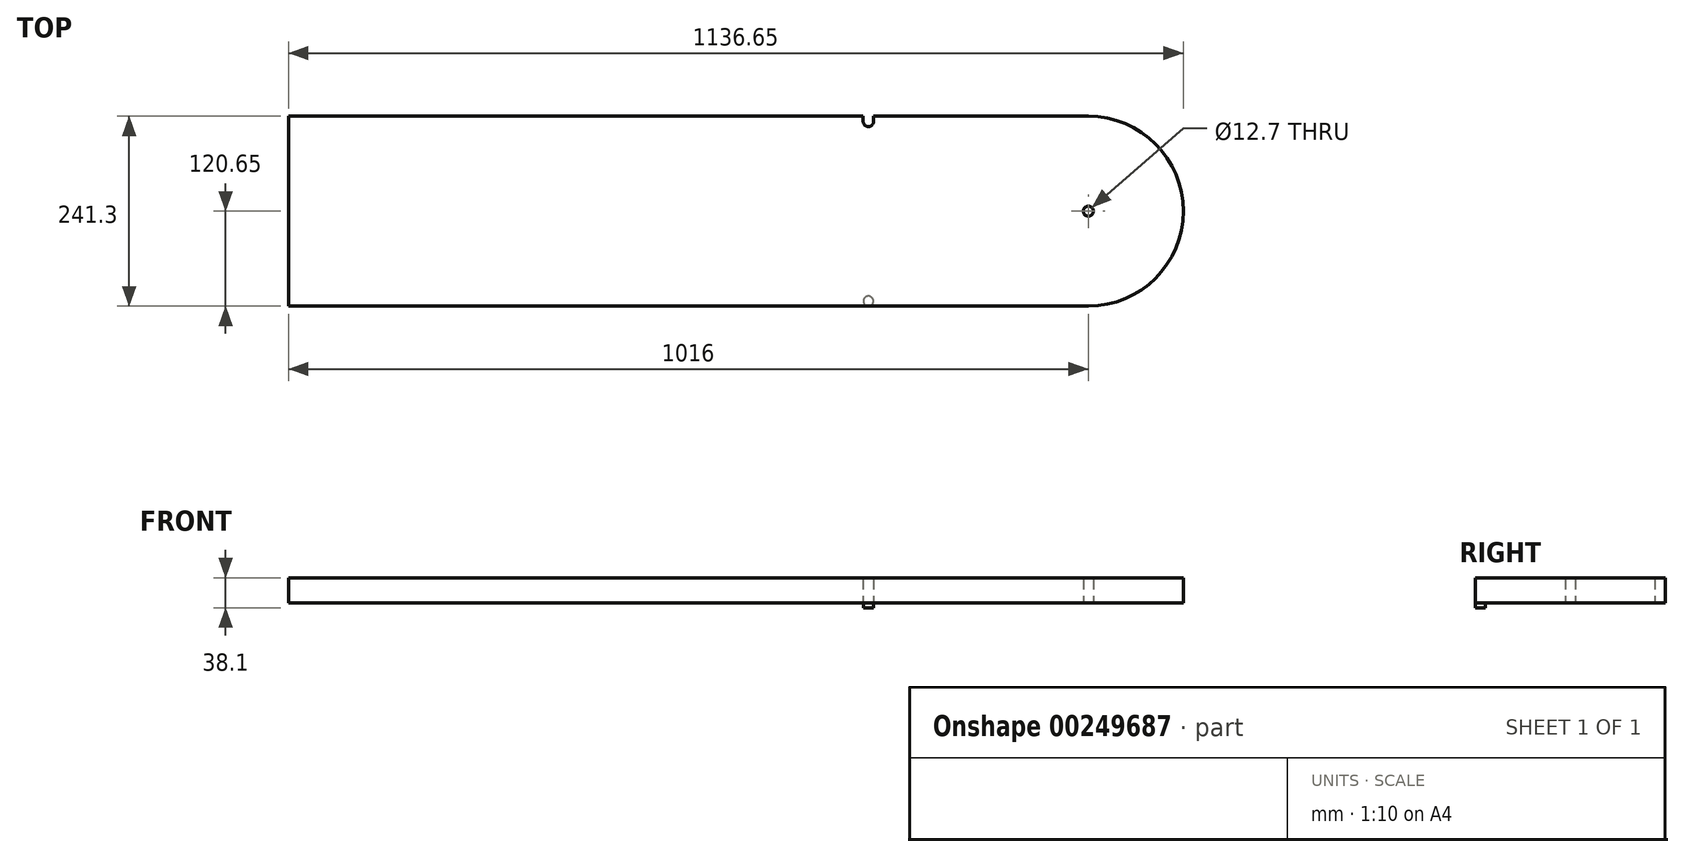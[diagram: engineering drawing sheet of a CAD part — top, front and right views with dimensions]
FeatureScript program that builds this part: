
annotation { "Feature Type Name" : "Feature", "Feature Type Description" : "" }
export const myFeature = defineFeature(function(context is Context, id is Id, definition is map)
    precondition{}
    {
        {
            var Q0;
            Q0=qCreatedBy(makeId("Top.planeOp"),FACE);
            var sketch = newSketch(context, id + "F0", { "sketchPlane" : qUnion([Q0])});
            skLineSegment(sketch, "E0.bottom", {"start": v(-1136.65, -120.65) * mm, "end": v(-120.65, -120.65) * mm});
            skLineSegment(sketch, "E0.top", {"start": v(-1136.65, 120.65) * mm, "end": v(-120.65, 120.65) * mm});
            skLineSegment(sketch, "E0.left", {"start": v(-1136.65, -120.65) * mm, "end": v(-1136.65, 120.65) * mm});
            skArc(sketch, "E1", {"start": v(-120.65, -120.65) * mm, "mid": v(0, 0) * mm, "end": v(-120.65, 120.65) * mm});
            skCircle(sketch, "E2", {"center": v(-120.65, 0) * mm, "radius": 6.35 * mm});
            skSolve(sketch);
        }
        {
            var Q0;
            Q0 = qSketchRegion(id + "F0", true);
            extrude(context, id + "F1", {"entities" : qUnion([Q0]), "depth" : 31.75 * mm});
        }
        {
            var Q0;
            Q0=makeQuery(id+"F1.opExtrude","CAP_FACE",FACE,{"disambiguationData":[OSD([sQuery(id+"F0.wireOp",EDGE,"E0.bottom"),sQuery(id+"F0.wireOp",EDGE,"E0.top"),sQuery(id+"F0.wireOp",EDGE,"E0.left"),sQuery(id+"F0.wireOp",EDGE,"E1"),sQuery(id+"F0.wireOp",EDGE,"E2")])],"isStart":true});
            var sketch = newSketch(context, id + "F2", { "sketchPlane" : qUnion([Q0])});
            skCircle(sketch, "E3", {"center": v(-400.05, 114.3) * mm, "radius": 6.35 * mm});
            skSolve(sketch);
        }
        {
            var Q0;
            Q0 = qSketchRegion(id + "F2", true);
            extrude(context, id + "F3", {"entities" : qUnion([Q0]), "operationType" : NewBodyOperationType.ADD, "depth" : 6.35 * mm});
        }
        {
            var Q0;
            Q0=makeQuery(id+"F1.opExtrude","CAP_FACE",FACE,{"disambiguationData":[OSD([sQuery(id+"F0.wireOp",EDGE,"E0.bottom"),sQuery(id+"F0.wireOp",EDGE,"E0.top"),sQuery(id+"F0.wireOp",EDGE,"E0.left"),sQuery(id+"F0.wireOp",EDGE,"E1"),sQuery(id+"F0.wireOp",EDGE,"E2")])],"isStart":true});
            var sketch = newSketch(context, id + "F4", { "sketchPlane" : qUnion([Q0])});
            skArc(sketch, "E4", {"start": v(-393.45, -114.05) * mm, "mid": v(-400.05, -107.44) * mm, "end": v(-406.65, -114.05) * mm});
            skLineSegment(sketch, "E5", {"start": v(-406.65, -114.05) * mm, "end": v(-406.65, -120.65) * mm});
            skLineSegment(sketch, "E6", {"start": v(-406.65, -120.65) * mm, "end": v(-393.45, -120.65) * mm});
            skLineSegment(sketch, "E7", {"start": v(-393.45, -120.65) * mm, "end": v(-393.45, -114.05) * mm});
            skSolve(sketch);
        }
        {
            var Q0;
            Q0 = qSketchRegion(id + "F4", true);
            extrude(context, id + "F5", {"entities" : qUnion([Q0]), "operationType" : NewBodyOperationType.REMOVE, "oppositeDirection" : true, "depth" : 31.75 * mm});
        }
    });
